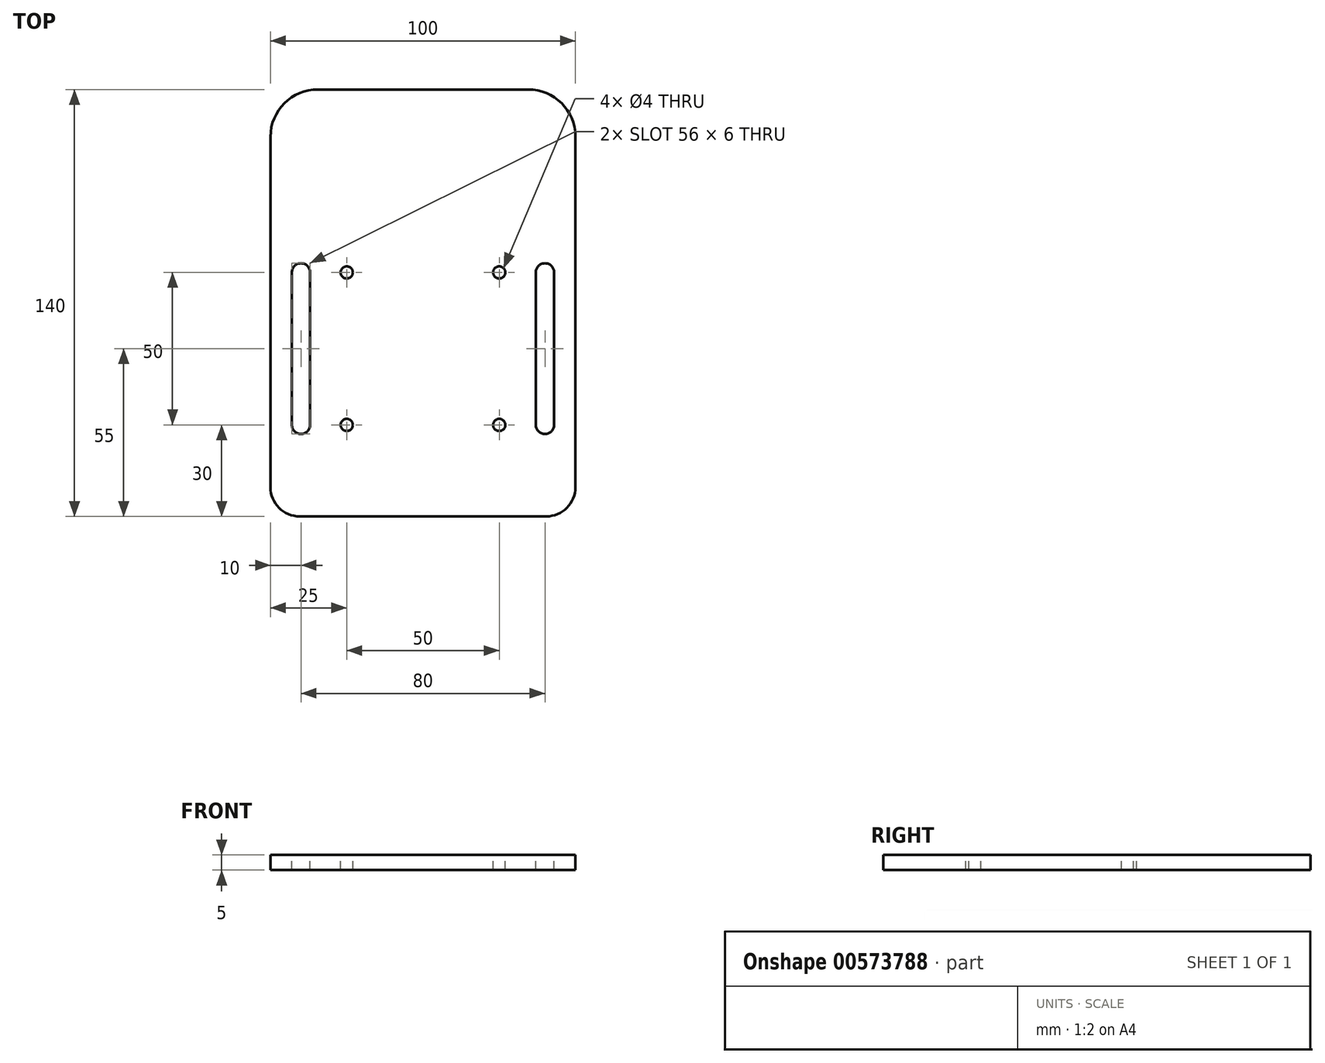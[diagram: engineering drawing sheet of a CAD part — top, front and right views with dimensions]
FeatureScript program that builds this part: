
annotation { "Feature Type Name" : "Feature", "Feature Type Description" : "" }
export const myFeature = defineFeature(function(context is Context, id is Id, definition is map)
    precondition{}
    {
        {
            var Q0;
            Q0=qCreatedBy(makeId("Top.planeOp"),FACE);
            var sketch = newSketch(context, id + "F0", { "sketchPlane" : qUnion([Q0])});
            skLineSegment(sketch, "E0.bottom", {"start": v(0, 0) * mm, "end": v(50, 0) * mm});
            skLineSegment(sketch, "E0.top", {"start": v(0, 140) * mm, "end": v(50, 140) * mm});
            skLineSegment(sketch, "E0.left", {"start": v(0, 0) * mm, "end": v(0, 140) * mm});
            skLineSegment(sketch, "E0.right", {"start": v(50, 0) * mm, "end": v(50, 140) * mm});
            skSolve(sketch);
        }
        {
            var Q0;
            Q0=makeQuery(id+"F0.imprint","IMPRINT",FACE,{"disambiguationData":[TD([[makeQuery(id+"F0.imprint","IMPRINT",EDGE,{"derivedFrom":sQuery(id+"F0.wireOp",EDGE,"E0.bottom")}),1.0]])]});
            extrude(context, id + "F1", {"entities" : qUnion([Q0]), "depth" : 5 * mm, "offsetDistance" : 25 * mm});
        }
        {
            var Q0;
            Q0=makeQuery(id+"F1.opExtrude","CAP_FACE",FACE,{"disambiguationData":[OSD([sQuery(id+"F0.wireOp",EDGE,"E0.bottom"),sQuery(id+"F0.wireOp",EDGE,"E0.top"),sQuery(id+"F0.wireOp",EDGE,"E0.left"),sQuery(id+"F0.wireOp",EDGE,"E0.right")])],"isStart":false});
            var sketch = newSketch(context, id + "F2", { "sketchPlane" : qUnion([Q0])});
            skLineSegment(sketch, "E1", {"start": v(25, 80) * mm, "end": v(25, 30) * mm});
            skSolve(sketch);
        }
        {
            var Q0;
            Q0=sQuery(id+"F2.wireOp",VERTEX,"E1.end");
            var Q1;
            Q1=sQuery(id+"F2.wireOp",VERTEX,"E1.start");
            var Q2;
            Q2=makeQuery(id+"F1.opExtrude","SWEPT_BODY",BODY,{"disambiguationData":[OSD([sQuery(id+"F0.wireOp",EDGE,"E0.bottom"),sQuery(id+"F0.wireOp",EDGE,"E0.top"),sQuery(id+"F0.wireOp",EDGE,"E0.left"),sQuery(id+"F0.wireOp",EDGE,"E0.right")])]});
            hole(context, id + "F3", {"style" : HoleStyle.SIMPLE, "endStyle" : HoleEndStyle.THROUGH, "holeDiameter" : 4 * mm, "isTappedThrough" : true, "tappedDepth" : 12 * mm, "tapClearance" : 3, "locations" : qUnion([Q0, Q1]), "scope" : qUnion([Q2])});
        }
        {
            var Q0;
            Q0=makeQuery(id+"F1.opExtrude","CAP_FACE",FACE,{"disambiguationData":[OSD([sQuery(id+"F0.wireOp",EDGE,"E0.bottom"),sQuery(id+"F0.wireOp",EDGE,"E0.top"),sQuery(id+"F0.wireOp",EDGE,"E0.left"),sQuery(id+"F0.wireOp",EDGE,"E0.right")])],"isStart":false});
            var sketch = newSketch(context, id + "F4", { "sketchPlane" : qUnion([Q0])});
            skLineSegment(sketch, "E2", {"start": v(40, 80) * mm, "end": v(40, 30) * mm});
            skLineSegment(sketch, "E3", {"start": v(40, 30) * mm, "end": v(40, 80) * mm});
            skSolve(sketch);
        }
        {
            var Q0;
            Q0=makeQuery(id+"F4.imprint","IMPRINT",FACE,{"disambiguationData":[TD([[makeQuery(id+"F4.imprint","IMPRINT",EDGE,{"derivedFrom":makeQuery(id+"F1.opExtrude","CAP_EDGE",EDGE,{"disambiguationData":[OSD([sQuery(id+"F0.wireOp",EDGE,"E0.bottom")])],"isStart":false})}),1.0]])]});
            var sketch = newSketch(context, id + "F5", { "sketchPlane" : qUnion([Q0])});
            skLineSegment(sketch, "E4.JUF.JUF", {"start": v(40, 30) * mm, "end": v(40, 80) * mm, "construction": true});
            skArc(sketch, "E4.0.startCap", {"start": v(43, 30) * mm, "mid": v(40, 27) * mm, "end": v(37, 30) * mm});
            skArc(sketch, "E4.0.endCap", {"start": v(37, 80) * mm, "mid": v(40, 83) * mm, "end": v(43, 80) * mm});
            skLineSegment(sketch, "E4.0.left", {"start": v(37, 30) * mm, "end": v(37, 80) * mm});
            skLineSegment(sketch, "E4.0.right", {"start": v(43, 30) * mm, "end": v(43, 80) * mm});
            skSolve(sketch);
        }
        {
            var Q0;
            Q0 = qSketchRegion(id + "F5", true);
            extrude(context, id + "F6", {"entities" : qUnion([Q0]), "operationType" : NewBodyOperationType.REMOVE, "oppositeDirection" : true, "depth" : 25 * mm, "offsetDistance" : 25 * mm});
        }
        {
            var Q0;
            Q0=makeQuery(id+"F1.opExtrude","SWEPT_EDGE",EDGE,{"disambiguationData":[OSD([sQuery(id+"F0.wireOp",EDGE,"E0.top"),sQuery(id+"F0.wireOp",EDGE,"E0.right")])]});
            fillet(context, id + "F7", {"entities" : qUnion([Q0]), "radius" : 15.53 * mm, "tangentPropagation" : true, "allowEdgeOverflow" : false});
        }
        {
            var Q0;
            Q0=makeQuery(id+"F1.opExtrude","SWEPT_EDGE",EDGE,{"disambiguationData":[OSD([sQuery(id+"F0.wireOp",EDGE,"E0.bottom"),sQuery(id+"F0.wireOp",EDGE,"E0.right")])]});
            fillet(context, id + "F8", {"entities" : qUnion([Q0]), "radius" : 9.6 * mm, "tangentPropagation" : true, "allowEdgeOverflow" : false});
        }
        {
            var Q0;
            Q0=makeQuery(id+"F1.opExtrude","SWEPT_BODY",BODY,{"disambiguationData":[OSD([sQuery(id+"F0.wireOp",EDGE,"E0.bottom"),sQuery(id+"F0.wireOp",EDGE,"E0.top"),sQuery(id+"F0.wireOp",EDGE,"E0.left"),sQuery(id+"F0.wireOp",EDGE,"E0.right")])]});
            var Q1;
            Q1=qCreatedBy(makeId("Right.planeOp"),FACE);
            mirror(context, id + "F9", {"operationType" : NewBodyOperationType.ADD, "entities" : qUnion([Q0]), "mirrorPlane" : qUnion([Q1])});
        }
    });
